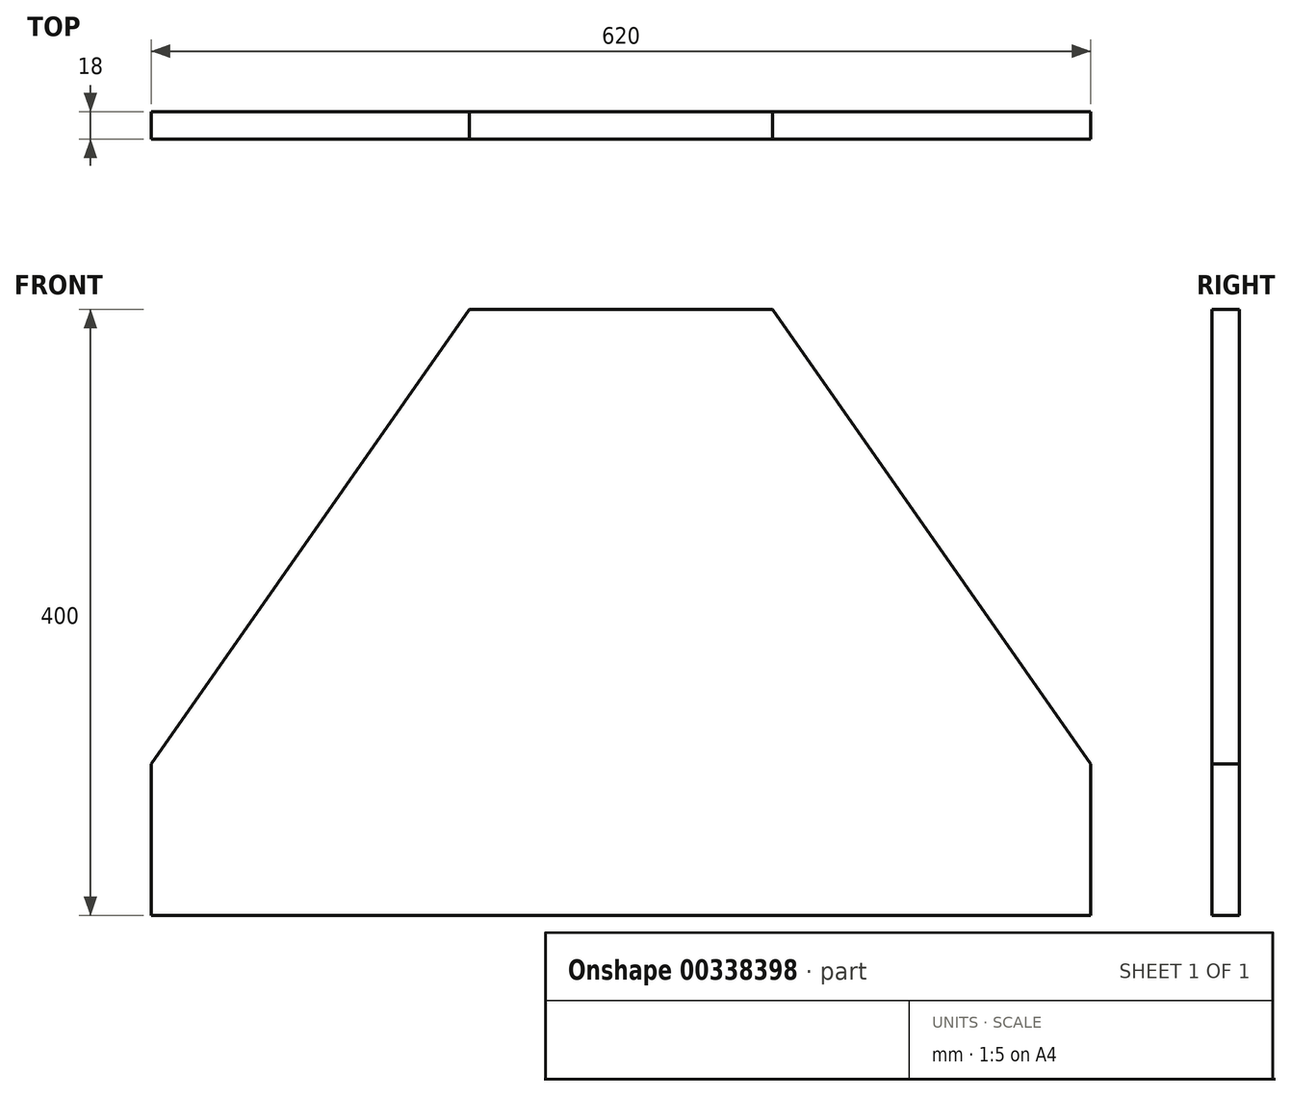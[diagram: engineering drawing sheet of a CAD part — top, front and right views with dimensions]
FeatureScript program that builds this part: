
annotation { "Feature Type Name" : "Feature", "Feature Type Description" : "" }
export const myFeature = defineFeature(function(context is Context, id is Id, definition is map)
    precondition{}
    {
        {
            var Q0;
            Q0=qCreatedBy(makeId("Front.planeOp"),FACE);
            var sketch = newSketch(context, id + "F0", { "sketchPlane" : qUnion([Q0])});
            skLineSegment(sketch, "E0.bottom", {"start": v(-100, -200) * mm, "end": v(100, -200) * mm});
            skLineSegment(sketch, "E0.top", {"start": v(-100, 200) * mm, "end": v(100, 200) * mm});
            skLineSegment(sketch, "E0.left", {"start": v(-100, -100) * mm, "end": v(-100, 200) * mm});
            skLineSegment(sketch, "E0.right", {"start": v(100, -100) * mm, "end": v(100, 200) * mm});
            skPoint(sketch, "E0.middle", {"position": v(0, 0) * mm});
            skLineSegment(sketch, "E1.bottom", {"start": v(-100, -200) * mm, "end": v(-310, -200) * mm});
            skLineSegment(sketch, "E1.top", {"start": v(-100, -100) * mm, "end": v(-310, -100) * mm});
            skLineSegment(sketch, "E1.right", {"start": v(-310, -200) * mm, "end": v(-310, -100) * mm});
            skLineSegment(sketch, "E2.bottom", {"start": v(100, -200) * mm, "end": v(310, -200) * mm});
            skLineSegment(sketch, "E2.top", {"start": v(100, -100) * mm, "end": v(310, -100) * mm});
            skLineSegment(sketch, "E2.right", {"start": v(310, -200) * mm, "end": v(310, -100) * mm});
            skLineSegment(sketch, "E3", {"start": v(-310, -100) * mm, "end": v(-100, 200) * mm});
            skLineSegment(sketch, "E4", {"start": v(100, 200) * mm, "end": v(310, -100) * mm});
            skSolve(sketch);
        }
        {
            var Q0;
            Q0=makeQuery(id+"F0.imprint","IMPRINT",FACE,{"disambiguationData":[TD([[makeQuery(id+"F0.imprint","IMPRINT",EDGE,{"derivedFrom":sQuery(id+"F0.wireOp",EDGE,"E0.right")}),-1.0]])]});
            var Q1;
            Q1=makeQuery(id+"F0.imprint","IMPRINT",FACE,{"disambiguationData":[TD([[makeQuery(id+"F0.imprint","IMPRINT",EDGE,{"derivedFrom":sQuery(id+"F0.wireOp",EDGE,"E0.bottom")}),1.0]])]});
            var Q2;
            Q2=makeQuery(id+"F0.imprint","IMPRINT",FACE,{"disambiguationData":[TD([[makeQuery(id+"F0.imprint","IMPRINT",EDGE,{"derivedFrom":sQuery(id+"F0.wireOp",EDGE,"E0.left")}),1.0]])]});
            extrude(context, id + "F1", {"entities" : qUnion([Q0, Q1, Q2]), "depth" : 18 * mm});
        }
    });
